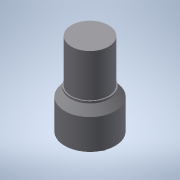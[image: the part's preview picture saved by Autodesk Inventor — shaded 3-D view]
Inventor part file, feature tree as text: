
AUTODESK INVENTOR PART (.ipt)
format: ipt  version: 2020 (Build 240168000, 168)  size: 195,072 bytes
history: native  units: mm
features: sketch x8, extrude x6, other x3, fillet x1
ambient origin geometry x8: Origin, YZ Plane, XZ Plane, XY Plane, X Axis, Y Axis, Z Axis, Center Point
bodies: Body1 (feature_tree)
feature tree (18):
  other  "實體1"
  extrude  "擠出1"  Depth=25.7mm
  extrude  "擠出2"  Depth=26.0mm TaperAngle=0.0deg
  other  "迴轉1"
  extrude  "擠出3"  Depth=20.0mm
  extrude  "擠出4"  Depth=1.0mm TaperAngle=0.0deg
  extrude  "擠出5"  Depth=4.0mm
  fillet  "圓角1"  [1 undecoded]
  other  "迴轉2"
  extrude  "擠出6"  Depth=10.0mm
  sketch  "草圖1"
  sketch  "草圖2"
  sketch  "草圖3"
  sketch  "草圖4"
  sketch  "草圖5"
  sketch  "草圖6"
  sketch  "草圖8"
  sketch  "草圖9"
note: 1 required parameter value undecoded (feature->parameter linkage not recoverable at this tier; creation-order binding heuristic only, values carry confidence <= 0.55)
